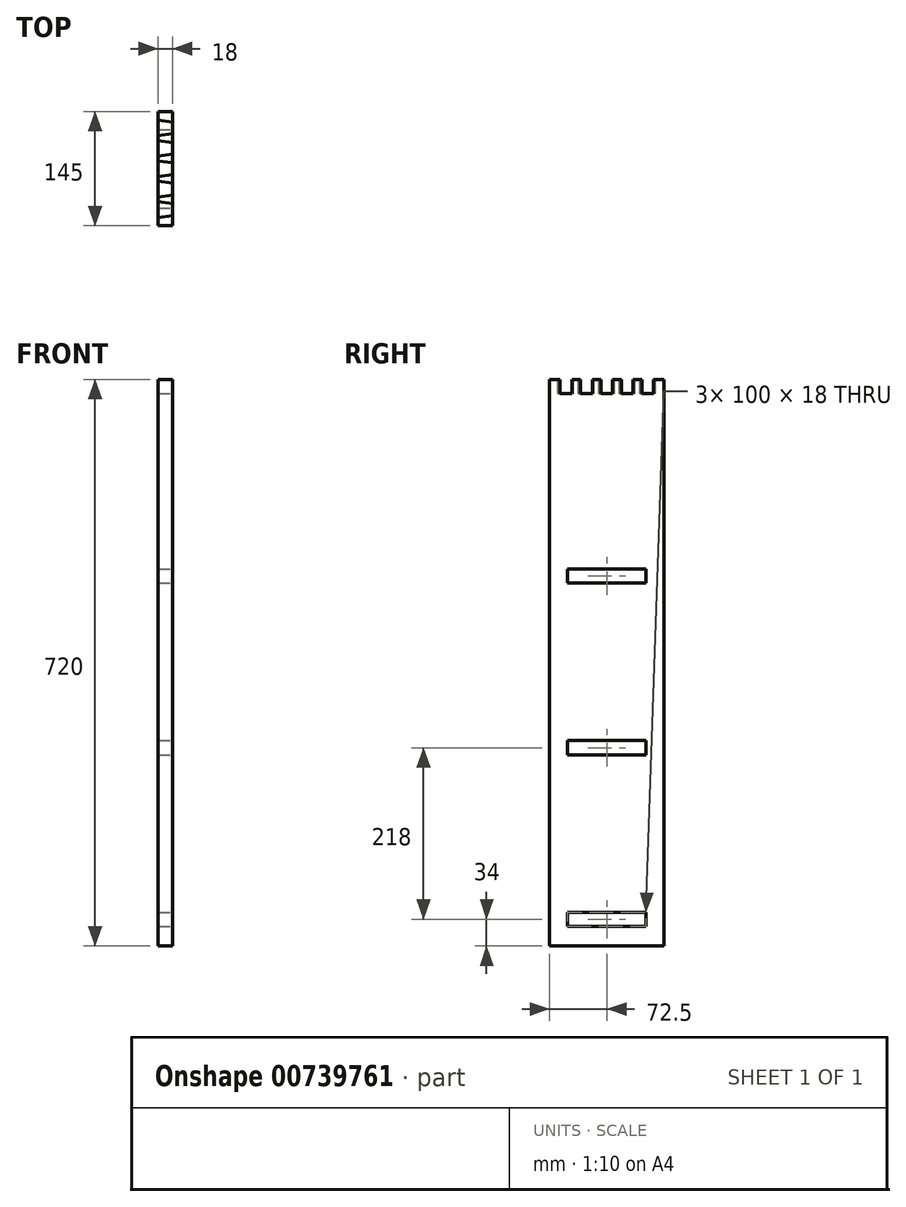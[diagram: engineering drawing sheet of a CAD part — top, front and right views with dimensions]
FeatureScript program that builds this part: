
annotation { "Feature Type Name" : "Feature", "Feature Type Description" : "" }
export const myFeature = defineFeature(function(context is Context, id is Id, definition is map)
    precondition{}
    {
        {
            var Q0;
            Q0=qCreatedBy(makeId("Top.planeOp"),FACE);
            var sketch = newSketch(context, id + "F0", { "sketchPlane" : qUnion([Q0])});
            skLineSegment(sketch, "E0.bottom", {"start": v(0, 72.5) * mm, "end": v(-18, 72.5) * mm});
            skLineSegment(sketch, "E0.top", {"start": v(0, -72.5) * mm, "end": v(-18, -72.5) * mm});
            skLineSegment(sketch, "E0.left", {"start": v(0, 72.5) * mm, "end": v(0, -72.5) * mm});
            skLineSegment(sketch, "E0.right", {"start": v(-18, 72.5) * mm, "end": v(-18, -72.5) * mm});
            skPoint(sketch, "E1", {"position": v(0, 0) * mm});
            skSolve(sketch);
        }
        {
            var Q0;
            Q0 = qSketchRegion(id + "F0", true);
            extrude(context, id + "F1", {"entities" : qUnion([Q0]), "depth" : 720 * mm, "offsetDistance" : 25 * mm});
        }
        {
            var Q0;
            Q0=makeQuery(id+"F1.opExtrude","SWEPT_FACE",FACE,{"disambiguationData":[OSD([sQuery(id+"F0.wireOp",EDGE,"E0.left")])]});
            var sketch = newSketch(context, id + "F2", { "sketchPlane" : qUnion([Q0])});
            skLineSegment(sketch, "E2.bottom", {"start": v(50, 25) * mm, "end": v(-50, 25) * mm});
            skLineSegment(sketch, "E2.top", {"start": v(50, 43) * mm, "end": v(-50, 43) * mm});
            skLineSegment(sketch, "E2.left", {"start": v(50, 25) * mm, "end": v(50, 43) * mm});
            skLineSegment(sketch, "E2.right", {"start": v(-50, 25) * mm, "end": v(-50, 43) * mm});
            skLineSegment(sketch, "E3.bottom", {"start": v(50, 243) * mm, "end": v(-50, 243) * mm});
            skLineSegment(sketch, "E3.top", {"start": v(50, 261) * mm, "end": v(-50, 261) * mm});
            skLineSegment(sketch, "E3.left", {"start": v(50, 243) * mm, "end": v(50, 261) * mm});
            skLineSegment(sketch, "E3.right", {"start": v(-50, 243) * mm, "end": v(-50, 261) * mm});
            skLineSegment(sketch, "E4.bottom", {"start": v(50, 461) * mm, "end": v(-50, 461) * mm});
            skLineSegment(sketch, "E4.top", {"start": v(50, 479) * mm, "end": v(-50, 479) * mm});
            skLineSegment(sketch, "E4.left", {"start": v(50, 461) * mm, "end": v(50, 479) * mm});
            skLineSegment(sketch, "E4.right", {"start": v(-50, 461) * mm, "end": v(-50, 479) * mm});
            skSolve(sketch);
        }
        {
            var Q0;
            Q0=makeQuery(id+"F2.imprint","IMPRINT",FACE,{"disambiguationData":[TD([[makeQuery(id+"F2.imprint","IMPRINT",EDGE,{"derivedFrom":sQuery(id+"F2.wireOp",EDGE,"E2.bottom")}),-1.0]])]});
            var Q1;
            Q1=makeQuery(id+"F2.imprint","IMPRINT",FACE,{"disambiguationData":[TD([[makeQuery(id+"F2.imprint","IMPRINT",EDGE,{"derivedFrom":sQuery(id+"F2.wireOp",EDGE,"E3.bottom")}),-1.0]])]});
            var Q2;
            Q2=makeQuery(id+"F2.imprint","IMPRINT",FACE,{"disambiguationData":[TD([[makeQuery(id+"F2.imprint","IMPRINT",EDGE,{"derivedFrom":sQuery(id+"F2.wireOp",EDGE,"E4.bottom")}),-1.0]])]});
            extrude(context, id + "F3", {"entities" : qUnion([Q0, Q1, Q2]), "operationType" : NewBodyOperationType.REMOVE, "endBound" : BoundingType.THROUGH_ALL, "oppositeDirection" : true, "depth" : 25 * mm, "offsetDistance" : 25 * mm});
        }
        {
            var Q0;
            Q0=makeQuery(id+"F1.opExtrude","CAP_FACE",FACE,{"disambiguationData":[OSD([sQuery(id+"F0.wireOp",EDGE,"E0.bottom"),sQuery(id+"F0.wireOp",EDGE,"E0.top"),sQuery(id+"F0.wireOp",EDGE,"E0.left"),sQuery(id+"F0.wireOp",EDGE,"E0.right")])],"isStart":false});
            var sketch = newSketch(context, id + "F4", { "sketchPlane" : qUnion([Q0])});
            skLineSegment(sketch, "E5", {"start": v(-18, 0) * mm, "end": v(-18, -10) * mm, "construction": true});
            skLineSegment(sketch, "E6", {"start": v(-18, 0) * mm, "end": v(0, 0) * mm, "construction": true});
            skLineSegment(sketch, "E7", {"start": v(-18, -10) * mm, "end": v(0, -7.5) * mm});
            skLineSegment(sketch, "E8", {"start": v(0, -7.5) * mm, "end": v(0, 0) * mm});
            skLineSegment(sketch, "E9", {"start": v(-18, -13) * mm, "end": v(0, -13) * mm, "construction": true});
            skLineSegment(sketch, "E10.MirrorCS", {"start": v(-18, -16) * mm, "end": v(0, -18.5) * mm});
            skLineSegment(sketch, "E11", {"start": v(-18, 0) * mm, "end": v(-18, -10) * mm});
            skLineSegment(sketch, "E12", {"start": v(-18, -26) * mm, "end": v(0, -26) * mm, "construction": true});
            skLineSegment(sketch, "E13.MirrorCS", {"start": v(-18, -36) * mm, "end": v(0, -33.5) * mm});
            skLineSegment(sketch, "E14", {"start": v(-18, -39) * mm, "end": v(0, -39) * mm, "construction": true});
            skLineSegment(sketch, "E15.MirrorCS", {"start": v(-18, -42) * mm, "end": v(0, -44.5) * mm});
            skLineSegment(sketch, "E16.MirrorCS", {"start": v(-18, -62) * mm, "end": v(0, -59.5) * mm});
            skLineSegment(sketch, "E17.MirrorCS", {"start": v(-18, 10) * mm, "end": v(0, 7.5) * mm});
            skLineSegment(sketch, "E18.MirrorCS", {"start": v(-18, 16) * mm, "end": v(0, 18.5) * mm});
            skLineSegment(sketch, "E19.MirrorCS", {"start": v(-18, 36) * mm, "end": v(0, 33.5) * mm});
            skLineSegment(sketch, "E20.MirrorCS", {"start": v(-18, 42) * mm, "end": v(0, 44.5) * mm});
            skLineSegment(sketch, "E21.MirrorCS", {"start": v(-18, 62) * mm, "end": v(0, 59.5) * mm});
            skLineSegment(sketch, "E22", {"start": v(0, 44.5) * mm, "end": v(0, 59.5) * mm});
            skLineSegment(sketch, "E23", {"start": v(-18, 42) * mm, "end": v(-18, 62) * mm});
            skLineSegment(sketch, "E24", {"start": v(-18, 36) * mm, "end": v(-18, 16) * mm});
            skLineSegment(sketch, "E25", {"start": v(0, 18.5) * mm, "end": v(0, 33.5) * mm});
            skLineSegment(sketch, "E26", {"start": v(-18, 10) * mm, "end": v(-18, 0) * mm});
            skLineSegment(sketch, "E27", {"start": v(0, 7.5) * mm, "end": v(0, 0) * mm});
            skLineSegment(sketch, "E28", {"start": v(-18, -42) * mm, "end": v(-18, -62) * mm});
            skLineSegment(sketch, "E29", {"start": v(0, -59.5) * mm, "end": v(0, -44.5) * mm});
            skLineSegment(sketch, "E30", {"start": v(0, -33.5) * mm, "end": v(0, -18.5) * mm});
            skLineSegment(sketch, "E31", {"start": v(-18, -36) * mm, "end": v(-18, -16) * mm});
            skSolve(sketch);
        }
        {
            var Q0;
            Q0=makeQuery(id+"F4.imprint","IMPRINT",FACE,{"disambiguationData":[TD([[makeQuery(id+"F4.imprint","IMPRINT",EDGE,{"derivedFrom":sQuery(id+"F4.wireOp",EDGE,"E7")}),1.0]])]});
            var Q1;
            Q1=makeQuery(id+"F4.imprint","IMPRINT",FACE,{"disambiguationData":[TD([[makeQuery(id+"F4.imprint","IMPRINT",EDGE,{"derivedFrom":sQuery(id+"F4.wireOp",EDGE,"E10.MirrorCS")}),-1.0]])]});
            var Q2;
            Q2=makeQuery(id+"F4.imprint","IMPRINT",FACE,{"disambiguationData":[TD([[makeQuery(id+"F4.imprint","IMPRINT",EDGE,{"derivedFrom":sQuery(id+"F4.wireOp",EDGE,"E19.MirrorCS")}),-1.0]])]});
            var Q3;
            Q3=makeQuery(id+"F4.imprint","IMPRINT",FACE,{"disambiguationData":[TD([[makeQuery(id+"F4.imprint","IMPRINT",EDGE,{"derivedFrom":sQuery(id+"F4.wireOp",EDGE,"E20.MirrorCS")}),1.0]])]});
            var Q4;
            Q4=makeQuery(id+"F4.imprint","IMPRINT",FACE,{"disambiguationData":[TD([[makeQuery(id+"F4.imprint","IMPRINT",EDGE,{"derivedFrom":sQuery(id+"F4.wireOp",EDGE,"E15.MirrorCS")}),-1.0]])]});
            extrude(context, id + "F5", {"entities" : qUnion([Q0, Q1, Q2, Q3, Q4]), "operationType" : NewBodyOperationType.REMOVE, "oppositeDirection" : true, "depth" : 18 * mm, "offsetDistance" : 25 * mm});
        }
    });
